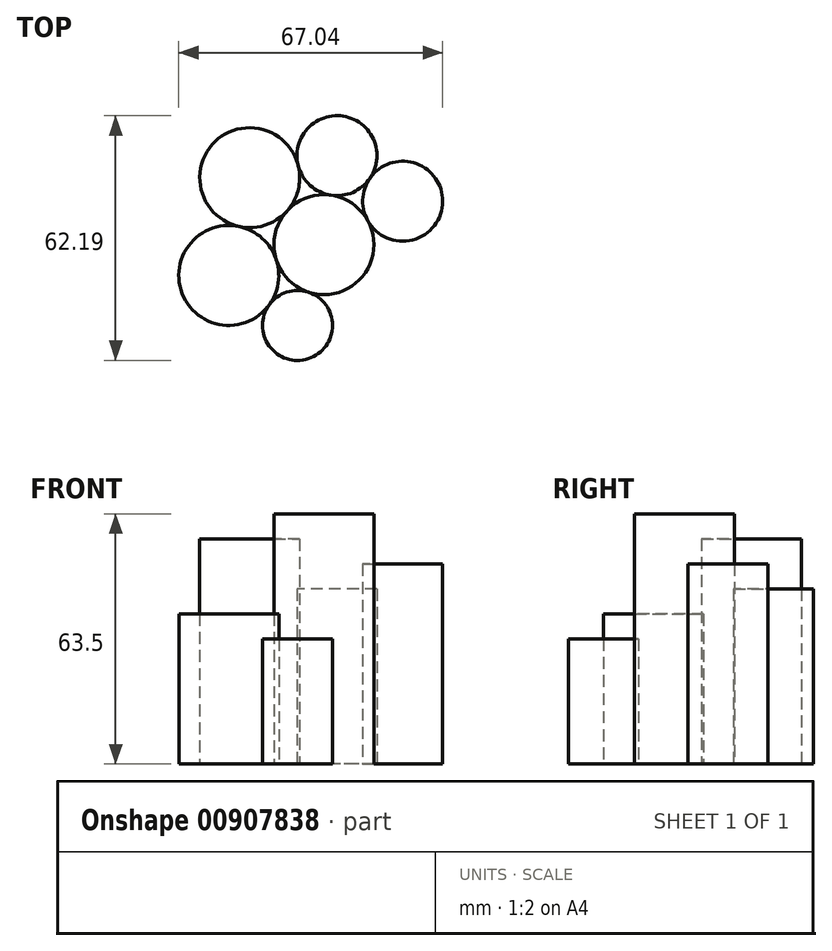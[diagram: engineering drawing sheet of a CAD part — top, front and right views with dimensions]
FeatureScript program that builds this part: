
annotation { "Feature Type Name" : "Feature", "Feature Type Description" : "" }
export const myFeature = defineFeature(function(context is Context, id is Id, definition is map)
    precondition{}
    {
        {
            var Q0;
            Q0=qCreatedBy(makeId("Top.planeOp"),FACE);
            var sketch = newSketch(context, id + "F0", { "sketchPlane" : qUnion([Q0])});
            skCircle(sketch, "E0", {"center": v(0, 0) * mm, "radius": 12.7 * mm});
            skCircle(sketch, "E1", {"center": v(-18.85, 17.02) * mm, "radius": 12.7 * mm});
            skCircle(sketch, "E2", {"center": v(-24.17, -7.82) * mm, "radius": 12.7 * mm});
            skCircle(sketch, "E3", {"center": v(-6.7, -20.52) * mm, "radius": 8.9 * mm});
            skCircle(sketch, "E4", {"center": v(20.01, 11.05) * mm, "radius": 10.16 * mm});
            skCircle(sketch, "E5", {"center": v(3.3, 22.62) * mm, "radius": 10.16 * mm});
            skSolve(sketch);
        }
        {
            var Q0;
            {var subQ0=sQuery(id+"F0.wireOp",EDGE,"E0");var subQ4=makeQuery(id+"F0.imprint","INTERSECT",VERTEX,{"derivedFrom":[subQ0,sQuery(id+"F0.wireOp",EDGE,"E5")]});Q0=makeQuery(id+"F0.imprint","IMPRINT",FACE,{"disambiguationData":[TD([[makeQuery(id+"F0.imprint","IMPRINT",EDGE,{"disambiguationData":[TD([[subQ4,1.0]])],"derivedFrom":subQ0}),1.0]])]});}
            extrude(context, id + "F1", {"entities" : qUnion([Q0]), "depth" : 63.5 * mm, "offsetDistance" : 25.4 * mm});
        }
        {
            var Q0;
            {var subQ0=sQuery(id+"F0.wireOp",EDGE,"E1");var subQ1=makeQuery(id+"F0.imprint","INTERSECT",VERTEX,{"derivedFrom":[subQ0,sQuery(id+"F0.wireOp",EDGE,"E2")]});Q0=makeQuery(id+"F0.imprint","IMPRINT",FACE,{"disambiguationData":[TD([[makeQuery(id+"F0.imprint","IMPRINT",EDGE,{"disambiguationData":[TD([[subQ1,1.0]])],"derivedFrom":subQ0}),1.0]])]});}
            extrude(context, id + "F2", {"entities" : qUnion([Q0]), "operationType" : NewBodyOperationType.ADD, "depth" : 57.15 * mm, "offsetDistance" : 25.4 * mm});
        }
        {
            var Q0;
            {var subQ0=sQuery(id+"F0.wireOp",EDGE,"E2");var subQ1=makeQuery(id+"F0.imprint","INTERSECT",VERTEX,{"derivedFrom":[sQuery(id+"F0.wireOp",EDGE,"E1"),subQ0]});Q0=makeQuery(id+"F0.imprint","IMPRINT",FACE,{"disambiguationData":[TD([[makeQuery(id+"F0.imprint","IMPRINT",EDGE,{"disambiguationData":[TD([[subQ1,1.0]])],"derivedFrom":subQ0}),1.0]])]});}
            extrude(context, id + "F3", {"entities" : qUnion([Q0]), "depth" : 38.1 * mm, "offsetDistance" : 25.4 * mm});
        }
        {
            var Q0;
            {var subQ0=sQuery(id+"F0.wireOp",EDGE,"E5");var subQ1=makeQuery(id+"F0.imprint","INTERSECT",VERTEX,{"derivedFrom":[sQuery(id+"F0.wireOp",EDGE,"E1"),subQ0]});Q0=makeQuery(id+"F0.imprint","IMPRINT",FACE,{"disambiguationData":[TD([[makeQuery(id+"F0.imprint","IMPRINT",EDGE,{"disambiguationData":[TD([[subQ1,-1.0]])],"derivedFrom":subQ0}),1.0]])]});}
            extrude(context, id + "F4", {"entities" : qUnion([Q0]), "depth" : 44.45 * mm, "offsetDistance" : 25.4 * mm});
        }
        {
            var Q0;
            {var subQ0=sQuery(id+"F0.wireOp",EDGE,"E4");var subQ1=makeQuery(id+"F0.imprint","INTERSECT",VERTEX,{"derivedFrom":[subQ0,sQuery(id+"F0.wireOp",EDGE,"E5")]});Q0=makeQuery(id+"F0.imprint","IMPRINT",FACE,{"disambiguationData":[TD([[makeQuery(id+"F0.imprint","IMPRINT",EDGE,{"disambiguationData":[TD([[subQ1,-1.0]])],"derivedFrom":subQ0}),1.0]])]});}
            var Q1;
            Q1=sQuery(id+"F0.wireOp",EDGE,"E4");
            extrude(context, id + "F5", {"entities" : qUnion([Q0]), "surfaceEntities" : qUnion([Q1]), "depth" : 50.8 * mm, "offsetDistance" : 25.4 * mm});
        }
        {
            var Q0;
            {var subQ0=sQuery(id+"F0.wireOp",EDGE,"E3");var subQ1=makeQuery(id+"F0.imprint","INTERSECT",VERTEX,{"derivedFrom":[sQuery(id+"F0.wireOp",EDGE,"E0"),subQ0]});Q0=makeQuery(id+"F0.imprint","IMPRINT",FACE,{"disambiguationData":[TD([[makeQuery(id+"F0.imprint","IMPRINT",EDGE,{"disambiguationData":[TD([[subQ1,-1.0]])],"derivedFrom":subQ0}),1.0]])]});}
            extrude(context, id + "F6", {"entities" : qUnion([Q0]), "depth" : 31.75 * mm, "offsetDistance" : 25.4 * mm});
        }
    });
